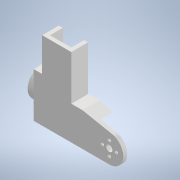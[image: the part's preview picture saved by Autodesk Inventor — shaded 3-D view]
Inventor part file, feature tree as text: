
AUTODESK INVENTOR PART (.ipt)
format: ipt  version: 2020 (Build 240168000, 168)  size: 220,160 bytes
history: native  units: mm
features: sketch x8, extrude x6, hole x2, shell x1
ambient origin geometry x8: Origin, YZ Plane, XZ Plane, XY Plane, X Axis, Y Axis, Z Axis, Center Point
bodies: Solid1 (feature_tree)
feature tree (17):
  extrude  "Extrusion1"  Depth=20.0mm
  shell  "Shell1"  Thickness=20.0mm
  extrude  "Extrusion2"  Depth=30.0mm TaperAngle=0.0deg
  extrude  "Extrusion3"  Depth=15.0mm
  hole  "Hole1"  [1 undecoded]
  extrude  "Extrusion4"  Depth=30.0mm TaperAngle=0.0deg
  extrude  "Extrusion5"  Depth=40.0mm
  hole  "Hole2"  [1 undecoded]
  extrude  "Extrusion6"  Depth=20.0mm
  sketch  "Sketch1"  dims[d4=52.0mm d6=58.0mm d7=20.0mm]
  sketch  "Sketch3"  dims[d8=80.0mm d9=30.0mm d10=0.0mm]
  sketch  "Sketch4"  dims[d12=120.0mm d14=15.0mm]
  sketch  "Sketch5"  dims[d15=80.0mm d16=52.0mm]
  sketch  "Sketch6"  dims[d17=60.0mm d19=30.0mm d20=0.0mm]
  sketch  "Sketch7"  dims[d21=7.0mm d22=40.0mm]
  sketch  "Sketch8"  dims[d23=20.0mm d24=0.0mm d25=25.0mm]
  sketch  "Sketch9"  dims[d26=3.4mm d27=6.0mm d28=6.3mm d29=2.0mm d30=90.0deg d31=20.0mm d32=0.0mm d33=4.0mm d34=6.5mm d36=4.0mm d37=4.0mm d38=5.5mm d39=8.0mm d40=40.0mm d42=360.0deg d44=10.0mm d45=0.0mm d46=81.0mm d47=0.0mm d48=0.0mm d49=25.0mm d50=3.4mm d51=6.0mm d52=6.3mm d53=2.0mm d54=90.0deg d55=20.0mm d56=0.0mm d57=11.0mm d58=0.0mm d59=0.0mm]
note: 2 required parameter values undecoded (feature->parameter linkage not recoverable at this tier; creation-order binding heuristic only, values carry confidence <= 0.55)
